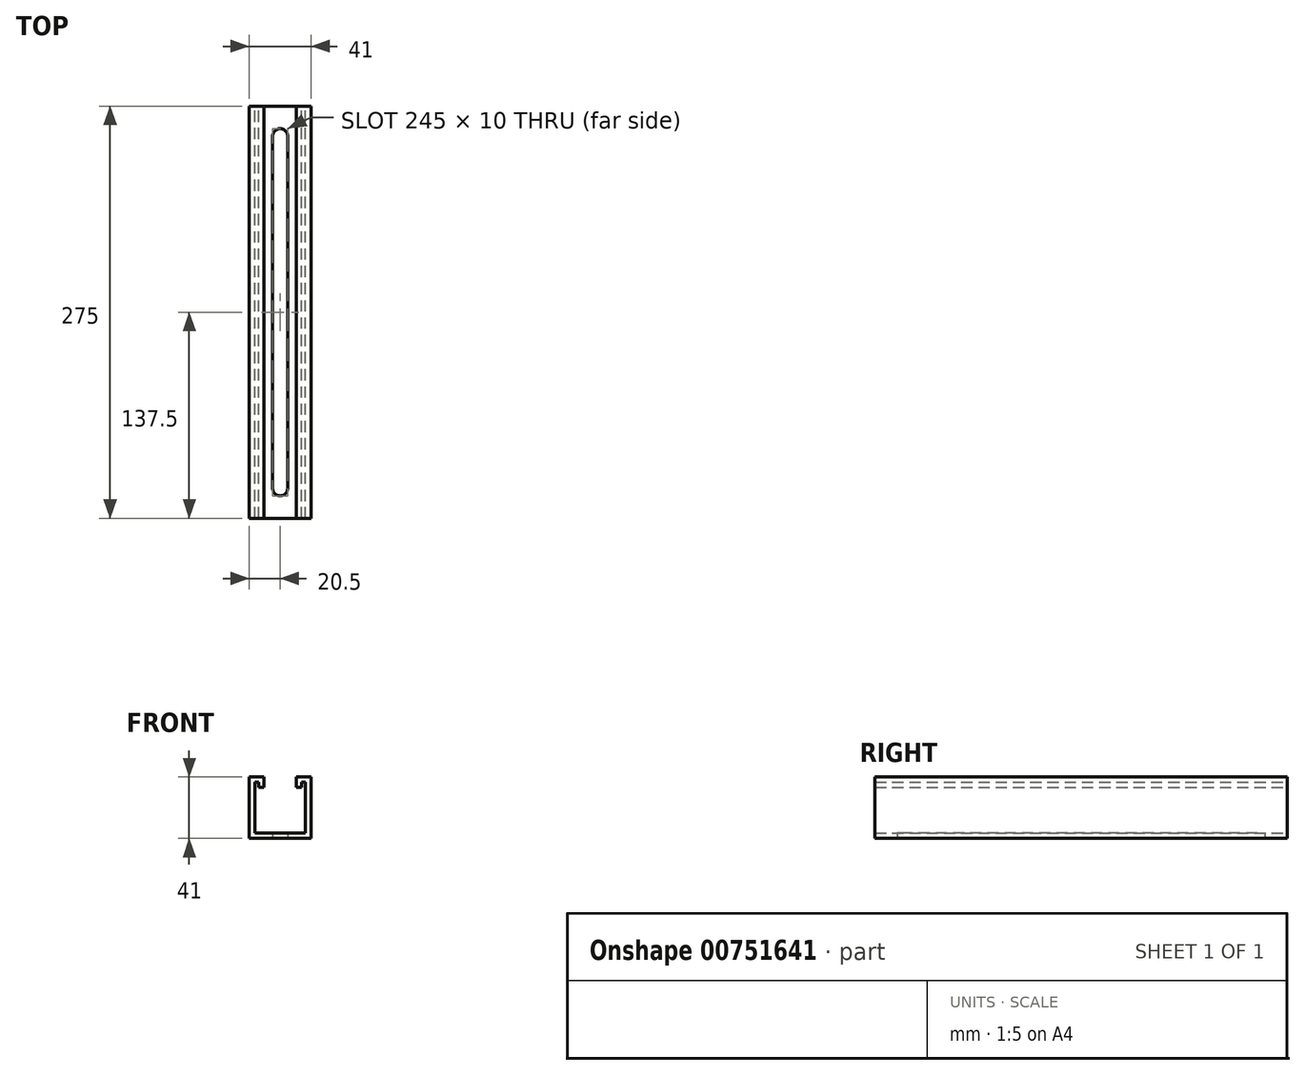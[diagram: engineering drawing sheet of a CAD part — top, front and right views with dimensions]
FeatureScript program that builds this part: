
annotation { "Feature Type Name" : "Feature", "Feature Type Description" : "" }
export const myFeature = defineFeature(function(context is Context, id is Id, definition is map)
    precondition{}
    {
        {
            var Q0;
            Q0=qCreatedBy(makeId("Front.planeOp"),FACE);
            var sketch = newSketch(context, id + "F0", { "sketchPlane" : qUnion([Q0])});
            skLineSegment(sketch, "E0", {"start": v(0, 0) * mm, "end": v(41, 0) * mm});
            skLineSegment(sketch, "E1", {"start": v(41, 0) * mm, "end": v(41, 41) * mm});
            skLineSegment(sketch, "E2", {"start": v(41, 41) * mm, "end": v(31.4, 41) * mm});
            skLineSegment(sketch, "E3", {"start": v(31.4, 41) * mm, "end": v(31.4, 34) * mm});
            skLineSegment(sketch, "E4", {"start": v(31.4, 34) * mm, "end": v(34.8, 34) * mm});
            skLineSegment(sketch, "E5", {"start": v(34.8, 34) * mm, "end": v(34.8, 37.5) * mm});
            skLineSegment(sketch, "E6", {"start": v(34.8, 37.5) * mm, "end": v(37.3, 37.5) * mm});
            skLineSegment(sketch, "E7", {"start": v(37.3, 37.5) * mm, "end": v(37.3, 3.7) * mm});
            skLineSegment(sketch, "E8", {"start": v(37.3, 3.7) * mm, "end": v(3.7, 3.7) * mm});
            skLineSegment(sketch, "E9", {"start": v(0, 0) * mm, "end": v(0, 41) * mm});
            skLineSegment(sketch, "E10", {"start": v(0, 41) * mm, "end": v(9.6, 41) * mm});
            skLineSegment(sketch, "E11", {"start": v(9.6, 41) * mm, "end": v(9.6, 34) * mm});
            skLineSegment(sketch, "E12", {"start": v(9.6, 34) * mm, "end": v(6.2, 34) * mm});
            skLineSegment(sketch, "E13", {"start": v(6.2, 34) * mm, "end": v(6.2, 37.5) * mm});
            skLineSegment(sketch, "E14", {"start": v(6.2, 37.5) * mm, "end": v(3.7, 37.5) * mm});
            skLineSegment(sketch, "E15", {"start": v(3.7, 37.5) * mm, "end": v(3.7, 3.7) * mm});
            skSolve(sketch);
        }
        {
            var Q0;
            Q0=qSketchRegion(id+"F0",true);
            extrude(context, id + "F1", {"entities" : qUnion([Q0]), "depth" : 275 * mm});
        }
        {
            var Q0;
            Q0=makeQuery(id+"F1.opExtrude","SWEPT_FACE",FACE,{"disambiguationData":[OSD([sQuery(id+"F0.wireOp",EDGE,"E0")])]});
            var sketch = newSketch(context, id + "F2", { "sketchPlane" : qUnion([Q0])});
            skArc(sketch, "E16", {"start": v(15.5, 20) * mm, "mid": v(20.5, 15) * mm, "end": v(25.5, 20) * mm});
            skPoint(sketch, "E16.centerSnap0", {"position": v(20.5, 0) * mm});
            skArc(sketch, "E17", {"start": v(25.5, 255) * mm, "mid": v(20.5, 260) * mm, "end": v(15.5, 255) * mm});
            skPoint(sketch, "E17.centerSnap0", {"position": v(20.5, 275) * mm});
            skLineSegment(sketch, "E18", {"start": v(25.5, 20) * mm, "end": v(25.5, 255) * mm});
            skLineSegment(sketch, "E19", {"start": v(15.5, 255) * mm, "end": v(15.5, 20) * mm});
            skSolve(sketch);
        }
        {
            var Q0;
            Q0=qSketchRegion(id+"F2",true);
            extrude(context, id + "F3", {"entities" : qUnion([Q0]), "operationType" : NewBodyOperationType.REMOVE, "endBound" : BoundingType.UP_TO_NEXT, "oppositeDirection" : true, "depth" : 25 * mm});
        }
    });
